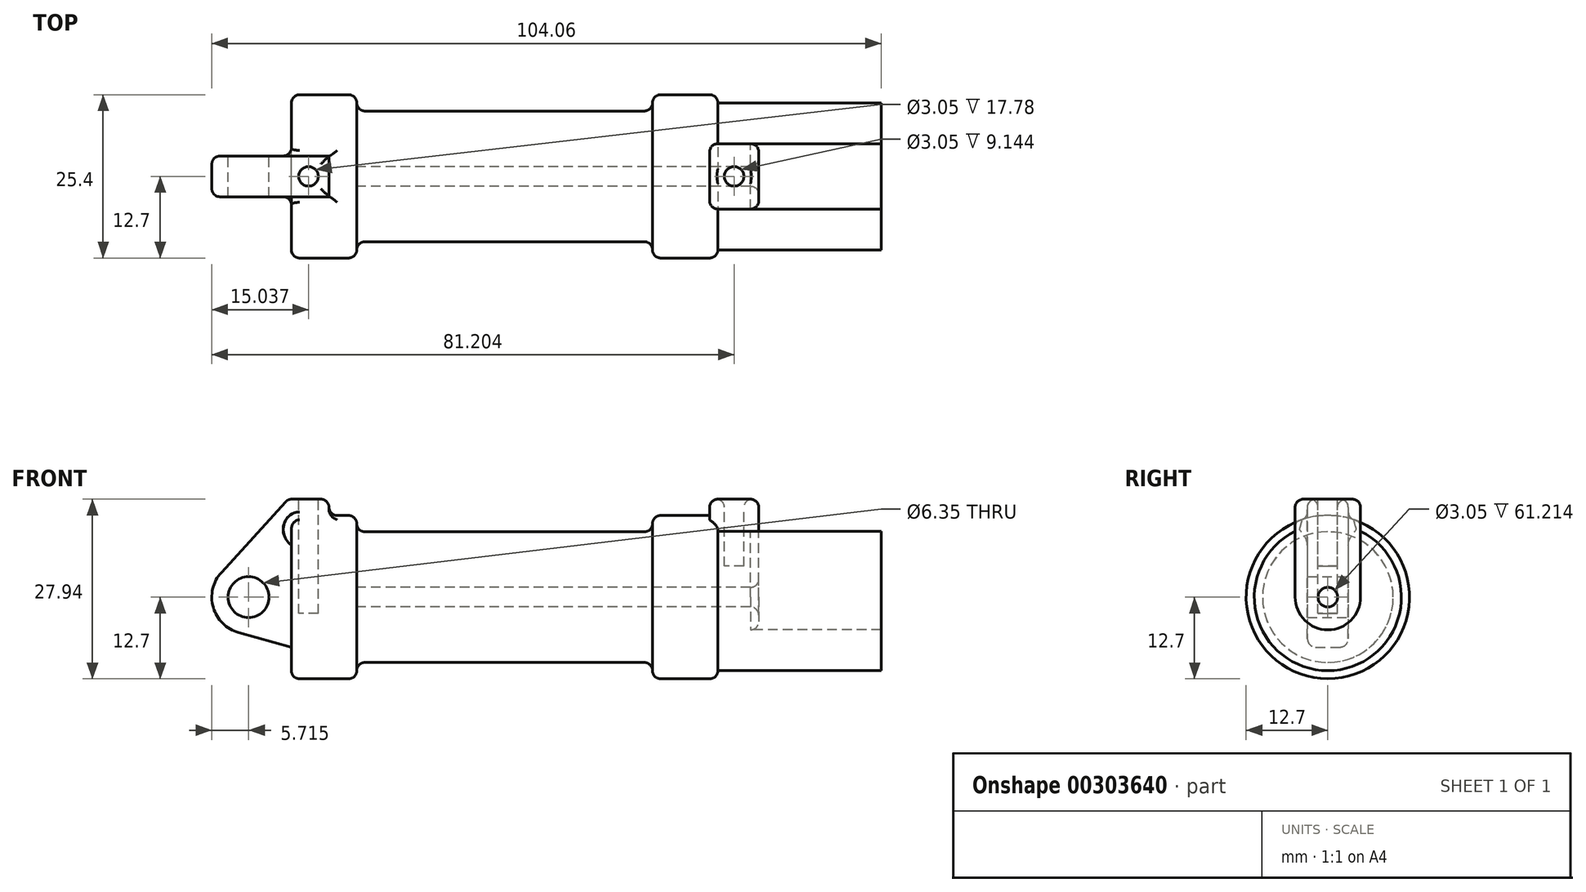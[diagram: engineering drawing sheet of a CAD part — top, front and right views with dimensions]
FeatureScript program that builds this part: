
annotation { "Feature Type Name" : "Feature", "Feature Type Description" : "" }
export const myFeature = defineFeature(function(context is Context, id is Id, definition is map)
    precondition{}
    {
        {
            var Q0;
            Q0=qCreatedBy(makeId("Front.planeOp"),FACE);
            var sketch = newSketch(context, id + "F0", { "sketchPlane" : qUnion([Q0])});
            skLineSegment(sketch, "E0", {"start": v(0, 0) * mm, "end": v(0, 12.7) * mm});
            skLineSegment(sketch, "E1", {"start": v(0, 12.7) * mm, "end": v(10.16, 12.7) * mm});
            skLineSegment(sketch, "E2", {"start": v(10.16, 12.7) * mm, "end": v(10.16, 10.16) * mm});
            skLineSegment(sketch, "E3", {"start": v(10.16, 10.16) * mm, "end": v(56.13, 10.16) * mm});
            skLineSegment(sketch, "E4", {"start": v(56.13, 10.16) * mm, "end": v(56.13, 12.7) * mm});
            skLineSegment(sketch, "E5", {"start": v(56.13, 12.7) * mm, "end": v(66.3, 12.7) * mm});
            skLineSegment(sketch, "E6", {"start": v(66.3, 12.7) * mm, "end": v(66.3, 0) * mm});
            skLineSegment(sketch, "E7", {"start": v(66.3, 0) * mm, "end": v(0, 0) * mm});
            skLineSegment(sketch, "E8", {"start": v(5.84, 15.24) * mm, "end": v(-0.5, 15.24) * mm});
            skLineSegment(sketch, "E9", {"start": v(-0.5, 15.24) * mm, "end": v(-10.88, 3.85) * mm});
            skLineSegment(sketch, "E10", {"start": v(0, 0) * mm, "end": v(-6.65, 0) * mm});
            skCircle(sketch, "E11", {"center": v(-6.65, 0) * mm, "radius": 5.72 * mm});
            skCircle(sketch, "E12", {"center": v(-6.65, 0) * mm, "radius": 3.18 * mm});
            skLineSegment(sketch, "E13", {"start": v(5.84, 15.24) * mm, "end": v(5.84, -9.4) * mm});
            skLineSegment(sketch, "E14", {"start": v(5.84, -9.4) * mm, "end": v(-8.18, -5.5) * mm});
            skSolve(sketch);
        }
        {
            var Q0;
            {var subQ0=sQuery(id+"F0.wireOp",EDGE,"E2");Q0=makeQuery(id+"F0.imprint","IMPRINT",FACE,{"disambiguationData":[TD([[makeQuery(id+"F0.imprint","IMPRINT",EDGE,{"derivedFrom":subQ0}),-1.0]])]});}
            var Q1;
            {var subQ0=sQuery(id+"F0.wireOp",EDGE,"E0");Q1=makeQuery(id+"F0.imprint","IMPRINT",FACE,{"disambiguationData":[TD([[makeQuery(id+"F0.imprint","IMPRINT",EDGE,{"derivedFrom":subQ0}),-1.0]])]});}
            var Q2;
            Q2=sQuery(id+"F0.wireOp",EDGE,"E7");
            revolve(context, id + "F1", {"entities" : qUnion([Q0, Q1]), "axis" : qUnion([Q2]), "revolveType" : RevolveType.FULL});
        }
        {
            var Q0;
            {var subQ1=sQuery(id+"F0.wireOp",EDGE,"E0");Q0=makeQuery(id+"F0.imprint","IMPRINT",FACE,{"disambiguationData":[TD([[makeQuery(id+"F0.imprint","IMPRINT",EDGE,{"derivedFrom":subQ1}),1.0]])]});}
            var Q1;
            {var subQ5=sQuery(id+"F0.wireOp",EDGE,"E12");Q1=makeQuery(id+"F0.imprint","IMPRINT",FACE,{"disambiguationData":[TD([[makeQuery(id+"F0.imprint","IMPRINT",EDGE,{"derivedFrom":subQ5}),-1.0]])]});}
            var Q2;
            {var subQ0=sQuery(id+"F0.wireOp",EDGE,"E14");Q2=makeQuery(id+"F0.imprint","IMPRINT",FACE,{"disambiguationData":[TD([[makeQuery(id+"F0.imprint","IMPRINT",EDGE,{"derivedFrom":subQ0}),-1.0]])]});}
            var Q3;
            {var subQ0=sQuery(id+"F0.wireOp",EDGE,"E0");Q3=makeQuery(id+"F0.imprint","IMPRINT",FACE,{"disambiguationData":[TD([[makeQuery(id+"F0.imprint","IMPRINT",EDGE,{"derivedFrom":subQ0}),-1.0]])]});}
            extrude(context, id + "F2", {"entities" : qUnion([Q0, Q1, Q2, Q3]), "operationType" : NewBodyOperationType.ADD, "depth" : 6.35 * mm, "symmetric" : true});
        }
        {
            var Q0;
            Q0=makeQuery(id+"F1.opRevolve","SWEPT_FACE",FACE,{"disambiguationData":[OSD([sQuery(id+"F0.wireOp",EDGE,"E6")])]});
            var sketch = newSketch(context, id + "F3", { "sketchPlane" : qUnion([Q0])});
            skCircle(sketch, "E15", {"center": v(0, 0) * mm, "radius": 1.52 * mm});
            skCircle(sketch, "E16", {"center": v(0, 0) * mm, "radius": 5.08 * mm});
            skLineSegment(sketch, "E17", {"start": v(-5.08, 0) * mm, "end": v(-5.08, 15.24) * mm});
            skLineSegment(sketch, "E18", {"start": v(5.08, 0) * mm, "end": v(5.08, 15.24) * mm});
            skLineSegment(sketch, "E19", {"start": v(-5.08, 15.24) * mm, "end": v(5.08, 15.24) * mm});
            skSolve(sketch);
        }
        {
            var Q0;
            {var subQ0=sQuery(id+"F3.wireOp",EDGE,"E19");Q0=makeQuery(id+"F3.imprint","IMPRINT",FACE,{"disambiguationData":[TD([[makeQuery(id+"F3.imprint","IMPRINT",EDGE,{"derivedFrom":subQ0}),-1.0]])]});}
            var Q1;
            {var subQ0=sQuery(id+"F3.wireOp",EDGE,"E17");var subQ1=sQuery(id+"F3.wireOp",EDGE,"E16");var subQ2=makeQuery(id+"F3.imprint","INTERSECT",VERTEX,{"derivedFrom":[subQ1,subQ0]});Q1=makeQuery(id+"F3.imprint","IMPRINT",FACE,{"disambiguationData":[TD([[makeQuery(id+"F3.imprint","IMPRINT",EDGE,{"disambiguationData":[TD([[subQ2,1.0]])],"derivedFrom":subQ1}),-1.0]])]});}
            var Q2;
            Q2=makeQuery(id+"F3.imprint","IMPRINT",FACE,{"disambiguationData":[TD([[makeQuery(id+"F3.imprint","IMPRINT",EDGE,{"derivedFrom":sQuery(id+"F3.wireOp",EDGE,"E15")}),-1.0]])]});
            extrude(context, id + "F4", {"entities" : qUnion([Q0, Q1, Q2]), "operationType" : NewBodyOperationType.ADD, "depth" : 6.35 * mm, "hasSecondDirection" : true, "secondDirectionOppositeDirection" : true, "secondDirectionDepth" : 1.27 * mm});
        }
        {
            var Q0;
            Q0=makeQuery(id+"F4.boolean.opBoolean","SPLIT",FACE,{"disambiguationData":[TD([makeQuery(id+"F4.opExtrude","SWEPT_FACE",FACE,{"disambiguationData":[OSD([sQuery(id+"F3.wireOp",EDGE,"E15")])]})])],"derivedFrom":makeQuery(id+"F1.opRevolve","SWEPT_FACE",FACE,{"disambiguationData":[OSD([sQuery(id+"F0.wireOp",EDGE,"E6")])]})});
            var Q1;
            Q1=makeQuery(id+"F1.opRevolve","SWEPT_FACE",FACE,{"disambiguationData":[OSD([sQuery(id+"F0.wireOp",EDGE,"E2")])]});
            extrude(context, id + "F5", {"entities" : qUnion([Q0]), "operationType" : NewBodyOperationType.REMOVE, "endBound" : BoundingType.UP_TO_SURFACE, "oppositeDirection" : true, "endBoundEntityFace" : qUnion([Q1]), "depth" : 25.4 * mm});
        }
        {
            var Q0;
            Q0=makeQuery(id+"F2.opExtrude","SWEPT_FACE",FACE,{"disambiguationData":[OSD([sQuery(id+"F0.wireOp",EDGE,"E8")])]});
            var sketch = newSketch(context, id + "F6", { "sketchPlane" : qUnion([Q0])});
            skCircle(sketch, "E20", {"center": v(2.67, 0) * mm, "radius": 1.52 * mm});
            skSolve(sketch);
        }
        {
            var Q0;
            Q0=makeQuery(id+"F4.opExtrude","SWEPT_FACE",FACE,{"disambiguationData":[OSD([sQuery(id+"F3.wireOp",EDGE,"E19")])]});
            var sketch = newSketch(context, id + "F7", { "sketchPlane" : qUnion([Q0])});
            skCircle(sketch, "E21", {"center": v(68.83, 0) * mm, "radius": 1.52 * mm});
            skSolve(sketch);
        }
        {
            var Q0;
            Q0=makeQuery(id+"F6.imprint","IMPRINT",FACE,{"disambiguationData":[TD([[makeQuery(id+"F6.imprint","IMPRINT",EDGE,{"derivedFrom":sQuery(id+"F6.wireOp",EDGE,"E20")}),1.0]])]});
            extrude(context, id + "F8", {"entities" : qUnion([Q0]), "operationType" : NewBodyOperationType.REMOVE, "oppositeDirection" : true, "depth" : 17.78 * mm});
        }
        {
            var Q0;
            Q0=makeQuery(id+"F7.imprint","IMPRINT",FACE,{"disambiguationData":[TD([[makeQuery(id+"F7.imprint","IMPRINT",EDGE,{"derivedFrom":sQuery(id+"F7.wireOp",EDGE,"E21")}),1.0]])]});
            extrude(context, id + "F9", {"entities" : qUnion([Q0]), "operationType" : NewBodyOperationType.REMOVE, "oppositeDirection" : true, "depth" : 10.4 * mm});
        }
        {
            var Q0;
            Q0=makeQuery(id+"F1.opRevolve","SWEPT_EDGE",EDGE,{"disambiguationData":[OSD([sQuery(id+"F0.wireOp",EDGE,"E5"),sQuery(id+"F0.wireOp",EDGE,"E6")])]});
            var Q1;
            Q1=makeQuery(id+"F1.opRevolve","SWEPT_EDGE",EDGE,{"disambiguationData":[OSD([sQuery(id+"F0.wireOp",EDGE,"E4"),sQuery(id+"F0.wireOp",EDGE,"E5")])]});
            var Q2;
            Q2=makeQuery(id+"F1.opRevolve","SWEPT_FACE",FACE,{"disambiguationData":[OSD([sQuery(id+"F0.wireOp",EDGE,"E3")])]});
            var Q3;
            Q3=makeQuery(id+"F1.opRevolve","SWEPT_FACE",FACE,{"disambiguationData":[OSD([sQuery(id+"F0.wireOp",EDGE,"E1")])]});
            var Q4;
            Q4=makeQuery(id+"F1.opRevolve","SWEPT_EDGE",EDGE,{"disambiguationData":[OSD([sQuery(id+"F0.wireOp",EDGE,"E0"),sQuery(id+"F0.wireOp",EDGE,"E1")])]});
            fillet(context, id + "F10", {"entities" : qUnion([Q0, Q1, Q2, Q3, Q4]), "radius" : 1.27 * mm, "tangentPropagation" : true, "allowEdgeOverflow" : false});
        }
        {
            var Q0;
            Q0=makeQuery(id+"F2.opExtrude","SWEPT_FACE",FACE,{"disambiguationData":[OSD([sQuery(id+"F0.wireOp",EDGE,"E9")])]});
            var Q1;
            Q1=makeQuery(id+"F2.opExtrude","CAP_EDGE",EDGE,{"disambiguationData":[OSD([sQuery(id+"F0.wireOp",EDGE,"E8")])],"isStart":true});
            var Q2;
            Q2=makeQuery(id+"F2.opExtrude","SWEPT_EDGE",EDGE,{"disambiguationData":[OSD([sQuery(id+"F0.wireOp",EDGE,"E8"),sQuery(id+"F0.wireOp",EDGE,"E13")])]});
            var Q3;
            Q3=makeQuery(id+"F2.opExtrude","CAP_EDGE",EDGE,{"disambiguationData":[OSD([sQuery(id+"F0.wireOp",EDGE,"E8")])],"isStart":false});
            fillet(context, id + "F11", {"entities" : qUnion([Q0, Q1, Q2, Q3]), "radius" : 1.27 * mm, "tangentPropagation" : true, "allowEdgeOverflow" : false});
        }
        {
            var Q0;
            Q0=makeQuery(id+"F4.opExtrude","CAP_FACE",FACE,{"disambiguationData":[OSD([sQuery(id+"F3.wireOp",EDGE,"E15"),sQuery(id+"F3.wireOp",EDGE,"E16"),sQuery(id+"F3.wireOp",EDGE,"E17"),sQuery(id+"F3.wireOp",EDGE,"E18"),sQuery(id+"F3.wireOp",EDGE,"E19")])],"isStart":false});
            var Q1;
            Q1=makeQuery(id+"F4.opExtrude","SWEPT_FACE",FACE,{"disambiguationData":[OSD([sQuery(id+"F3.wireOp",EDGE,"E19")])]});
            var Q2;
            Q2=makeQuery(id+"F4.opExtrude","CAP_EDGE",EDGE,{"disambiguationData":[OSD([sQuery(id+"F3.wireOp",EDGE,"E17")])],"isStart":true});
            var Q3;
            Q3=makeQuery(id+"F4.opExtrude","CAP_EDGE",EDGE,{"disambiguationData":[OSD([sQuery(id+"F3.wireOp",EDGE,"E18")])],"isStart":true});
            fillet(context, id + "F12", {"entities" : qUnion([Q0, Q1, Q2, Q3]), "radius" : 1.27 * mm, "tangentPropagation" : true, "allowEdgeOverflow" : false});
        }
        {
            var Q0;
            {var subQ0=sQuery(id+"FXvLCQylG0OJOqs_1.wireOp",EDGE,"3RpC5Bgf-b7m6-Ug9A-TNXq-2KlfdZ5rkiCp");Q0=makeQuery(id+"FXvLCQylG0OJOqs_1.imprint","IMPRINT",FACE,{"disambiguationData":[TD([[makeQuery(id+"FXvLCQylG0OJOqs_1.imprint","IMPRINT",EDGE,{"derivedFrom":subQ0}),-1.0]])]});}
            var Q1;
            Q1=makeQuery(id+"F1.opRevolve","SWEPT_FACE",FACE,{"disambiguationData":[OSD([sQuery(id+"F0.wireOp",EDGE,"E6")])]});
            extrude(context, id + "F13", {"entities" : qUnion([Q0, Q1]), "operationType" : NewBodyOperationType.ADD, "depth" : 25.4 * mm});
        }
    });
